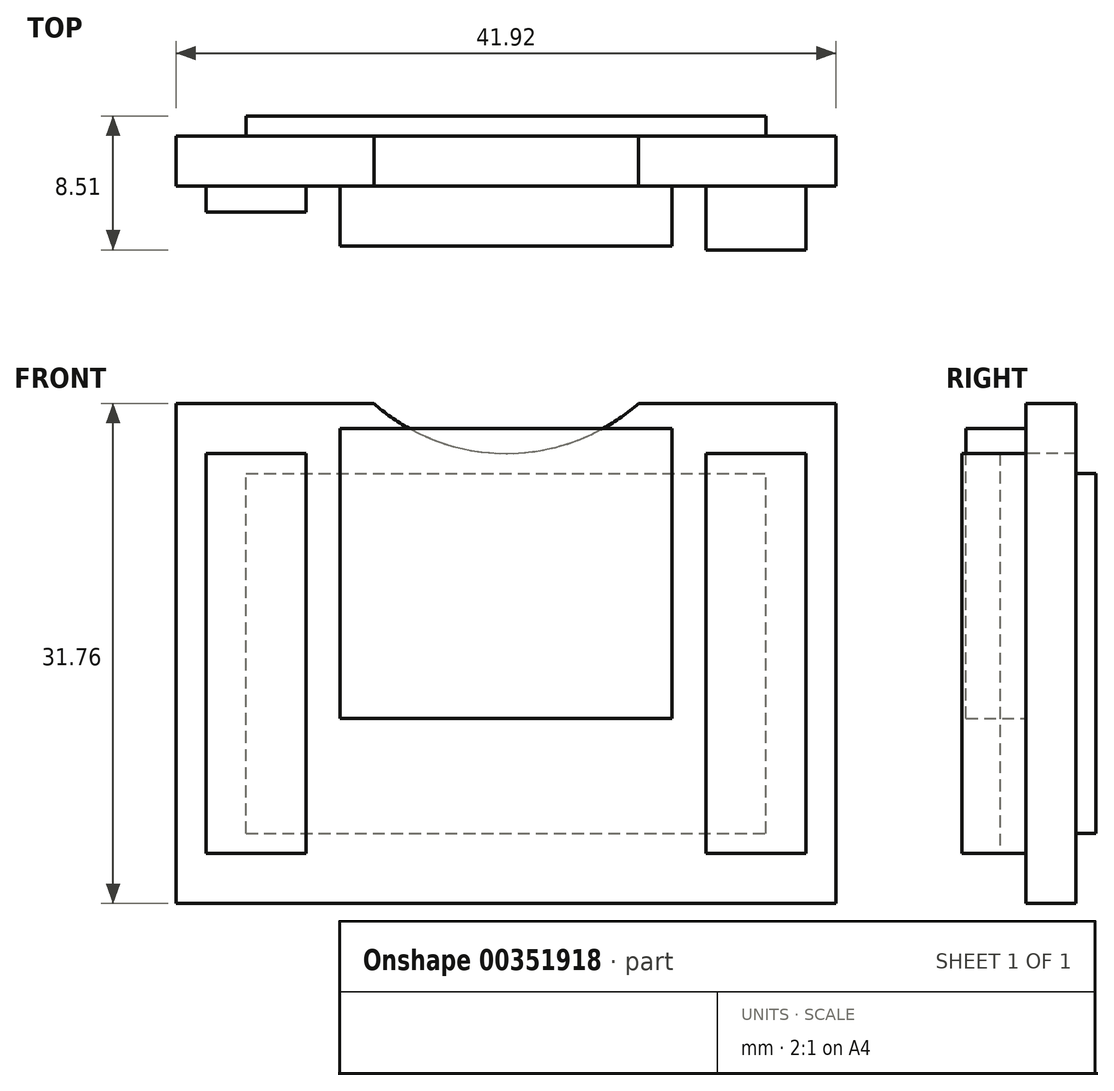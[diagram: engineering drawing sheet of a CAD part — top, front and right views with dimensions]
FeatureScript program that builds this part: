
annotation { "Feature Type Name" : "Feature", "Feature Type Description" : "" }
export const myFeature = defineFeature(function(context is Context, id is Id, definition is map)
    precondition{}
    {
        {
            var Q0;
            Q0=qCreatedBy(makeId("Front.planeOp"),FACE);
            var sketch = newSketch(context, id + "F0", { "sketchPlane" : qUnion([Q0])});
            skLineSegment(sketch, "E0.bottom", {"start": v(20.96, -15.87) * mm, "end": v(-20.96, -15.88) * mm});
            skLineSegment(sketch, "E0.top", {"start": v(20.96, 15.88) * mm, "end": v(-20.96, 15.87) * mm});
            skLineSegment(sketch, "E0.left", {"start": v(20.96, -15.88) * mm, "end": v(20.96, 15.88) * mm});
            skLineSegment(sketch, "E0.right", {"start": v(-20.96, -15.88) * mm, "end": v(-20.96, 15.87) * mm});
            skPoint(sketch, "E0.middle", {"position": v(0, 0) * mm});
            skSolve(sketch);
        }
        {
            var Q0;
            Q0=makeQuery(id+"F0.imprint","IMPRINT",FACE,{"disambiguationData":[TD([[makeQuery(id+"F0.imprint","IMPRINT",EDGE,{"derivedFrom":sQuery(id+"F0.wireOp",EDGE,"E0.bottom")}),-1.0]])]});
            extrude(context, id + "F1", {"entities" : qUnion([Q0]), "depth" : 3.17 * mm});
        }
        {
            var Q0;
            Q0=makeQuery(id+"F1.opExtrude","CAP_FACE",FACE,{"disambiguationData":[OSD([sQuery(id+"F0.wireOp",EDGE,"E0.bottom"),sQuery(id+"F0.wireOp",EDGE,"E0.top"),sQuery(id+"F0.wireOp",EDGE,"E0.left"),sQuery(id+"F0.wireOp",EDGE,"E0.right")])],"isStart":false});
            var sketch = newSketch(context, id + "F2", { "sketchPlane" : qUnion([Q0])});
            skSolve(sketch);
        }
        {
            var Q0;
            Q0=makeQuery(id+"F2.imprint","IMPRINT",FACE,{"disambiguationData":[TD([[makeQuery(id+"F2.imprint","IMPRINT",EDGE,{"derivedFrom":makeQuery(id+"F1.opExtrude","CAP_EDGE",EDGE,{"disambiguationData":[OSD([sQuery(id+"F0.wireOp",EDGE,"E0.bottom")])],"isStart":false})}),-1.0]])]});
            var sketch = newSketch(context, id + "F3", { "sketchPlane" : qUnion([Q0])});
            skLineSegment(sketch, "E1.0", {"start": v(20.96, 15.88) * mm, "end": v(-20.96, 15.87) * mm});
            skArc(sketch, "E2", {"start": v(-8.4, 15.87) * mm, "mid": v(0, 12.7) * mm, "end": v(8.4, 15.87) * mm});
            skSolve(sketch);
        }
        {
            var Q0;
            {var subQ0=sQuery(id+"F3.wireOp",EDGE,"E2");Q0=makeQuery(id+"F3.imprint","IMPRINT",FACE,{"disambiguationData":[TD([[makeQuery(id+"F3.imprint","IMPRINT",EDGE,{"derivedFrom":subQ0}),1.0]])]});}
            extrude(context, id + "F4", {"entities" : qUnion([Q0]), "operationType" : NewBodyOperationType.REMOVE, "endBound" : BoundingType.THROUGH_ALL, "oppositeDirection" : true, "depth" : 25.4 * mm});
        }
        {
            var Q0;
            Q0=makeQuery(id+"F2.imprint","IMPRINT",FACE,{"disambiguationData":[TD([[makeQuery(id+"F2.imprint","IMPRINT",EDGE,{"derivedFrom":makeQuery(id+"F1.opExtrude","CAP_EDGE",EDGE,{"disambiguationData":[OSD([sQuery(id+"F0.wireOp",EDGE,"E0.bottom")])],"isStart":false})}),-1.0]])]});
            var sketch = newSketch(context, id + "F5", { "sketchPlane" : qUnion([Q0])});
            skLineSegment(sketch, "E3.bottom", {"start": v(10.54, -4.13) * mm, "end": v(-10.54, -4.13) * mm});
            skLineSegment(sketch, "E3.top", {"start": v(10.54, 14.29) * mm, "end": v(-10.54, 14.29) * mm});
            skLineSegment(sketch, "E3.left", {"start": v(10.54, -4.13) * mm, "end": v(10.54, 14.29) * mm});
            skLineSegment(sketch, "E3.right", {"start": v(-10.54, -4.13) * mm, "end": v(-10.54, 14.29) * mm});
            skPoint(sketch, "E3.middle", {"position": v(0, 5.08) * mm});
            skSolve(sketch);
        }
        {
            var Q0;
            Q0 = qSketchRegion(id + "F5", true);
            extrude(context, id + "F6", {"entities" : qUnion([Q0]), "operationType" : NewBodyOperationType.ADD, "depth" : 3.8 * mm});
        }
        {
            var Q0;
            Q0=makeQuery(id+"F2.imprint","IMPRINT",FACE,{"disambiguationData":[TD([[makeQuery(id+"F2.imprint","IMPRINT",EDGE,{"derivedFrom":makeQuery(id+"F1.opExtrude","CAP_EDGE",EDGE,{"disambiguationData":[OSD([sQuery(id+"F0.wireOp",EDGE,"E0.bottom")])],"isStart":false})}),-1.0]])]});
            var sketch = newSketch(context, id + "F7", { "sketchPlane" : qUnion([Q0])});
            skLineSegment(sketch, "E4.bottom", {"start": v(12.7, 12.7) * mm, "end": v(19.05, 12.7) * mm});
            skLineSegment(sketch, "E4.top", {"start": v(12.7, -12.7) * mm, "end": v(19.05, -12.7) * mm});
            skLineSegment(sketch, "E4.left", {"start": v(12.7, 12.7) * mm, "end": v(12.7, -12.7) * mm});
            skLineSegment(sketch, "E4.right", {"start": v(19.05, 12.7) * mm, "end": v(19.05, -12.7) * mm});
            skSolve(sketch);
        }
        {
            var Q0;
            Q0 = qSketchRegion(id + "F7", true);
            extrude(context, id + "F8", {"entities" : qUnion([Q0]), "operationType" : NewBodyOperationType.ADD, "depth" : 4.06 * mm});
        }
        {
            var Q0;
            Q0=makeQuery(id+"F2.imprint","IMPRINT",FACE,{"disambiguationData":[TD([[makeQuery(id+"F2.imprint","IMPRINT",EDGE,{"derivedFrom":makeQuery(id+"F1.opExtrude","CAP_EDGE",EDGE,{"disambiguationData":[OSD([sQuery(id+"F0.wireOp",EDGE,"E0.bottom")])],"isStart":false})}),-1.0]])]});
            var sketch = newSketch(context, id + "F9", { "sketchPlane" : qUnion([Q0])});
            skLineSegment(sketch, "E5.bottom", {"start": v(-19.05, 12.7) * mm, "end": v(-12.7, 12.7) * mm});
            skLineSegment(sketch, "E5.top", {"start": v(-19.05, -12.7) * mm, "end": v(-12.7, -12.7) * mm});
            skLineSegment(sketch, "E5.left", {"start": v(-19.05, 12.7) * mm, "end": v(-19.05, -12.7) * mm});
            skLineSegment(sketch, "E5.right", {"start": v(-12.7, 12.7) * mm, "end": v(-12.7, -12.7) * mm});
            skSolve(sketch);
        }
        {
            var Q0;
            Q0 = qSketchRegion(id + "F9", true);
            extrude(context, id + "F10", {"entities" : qUnion([Q0]), "operationType" : NewBodyOperationType.ADD, "depth" : 1.65 * mm});
        }
        {
            var Q0;
            Q0=makeQuery(id+"F1.opExtrude","CAP_FACE",FACE,{"disambiguationData":[OSD([sQuery(id+"F0.wireOp",EDGE,"E0.bottom"),sQuery(id+"F0.wireOp",EDGE,"E0.top"),sQuery(id+"F0.wireOp",EDGE,"E0.left"),sQuery(id+"F0.wireOp",EDGE,"E0.right")])],"isStart":true});
            var sketch = newSketch(context, id + "F11", { "sketchPlane" : qUnion([Q0])});
            skLineSegment(sketch, "E6.bottom", {"start": v(16.51, -11.43) * mm, "end": v(-16.51, -11.43) * mm});
            skLineSegment(sketch, "E6.top", {"start": v(16.51, 11.43) * mm, "end": v(-16.51, 11.43) * mm});
            skLineSegment(sketch, "E6.left", {"start": v(16.51, -11.43) * mm, "end": v(16.51, 11.43) * mm});
            skLineSegment(sketch, "E6.right", {"start": v(-16.51, -11.43) * mm, "end": v(-16.51, 11.43) * mm});
            skPoint(sketch, "E6.middle", {"position": v(0, 0) * mm});
            skSolve(sketch);
        }
        {
            var Q0;
            Q0 = qSketchRegion(id + "F11", true);
            extrude(context, id + "F12", {"entities" : qUnion([Q0]), "operationType" : NewBodyOperationType.ADD, "depth" : 1.27 * mm});
        }
    });
